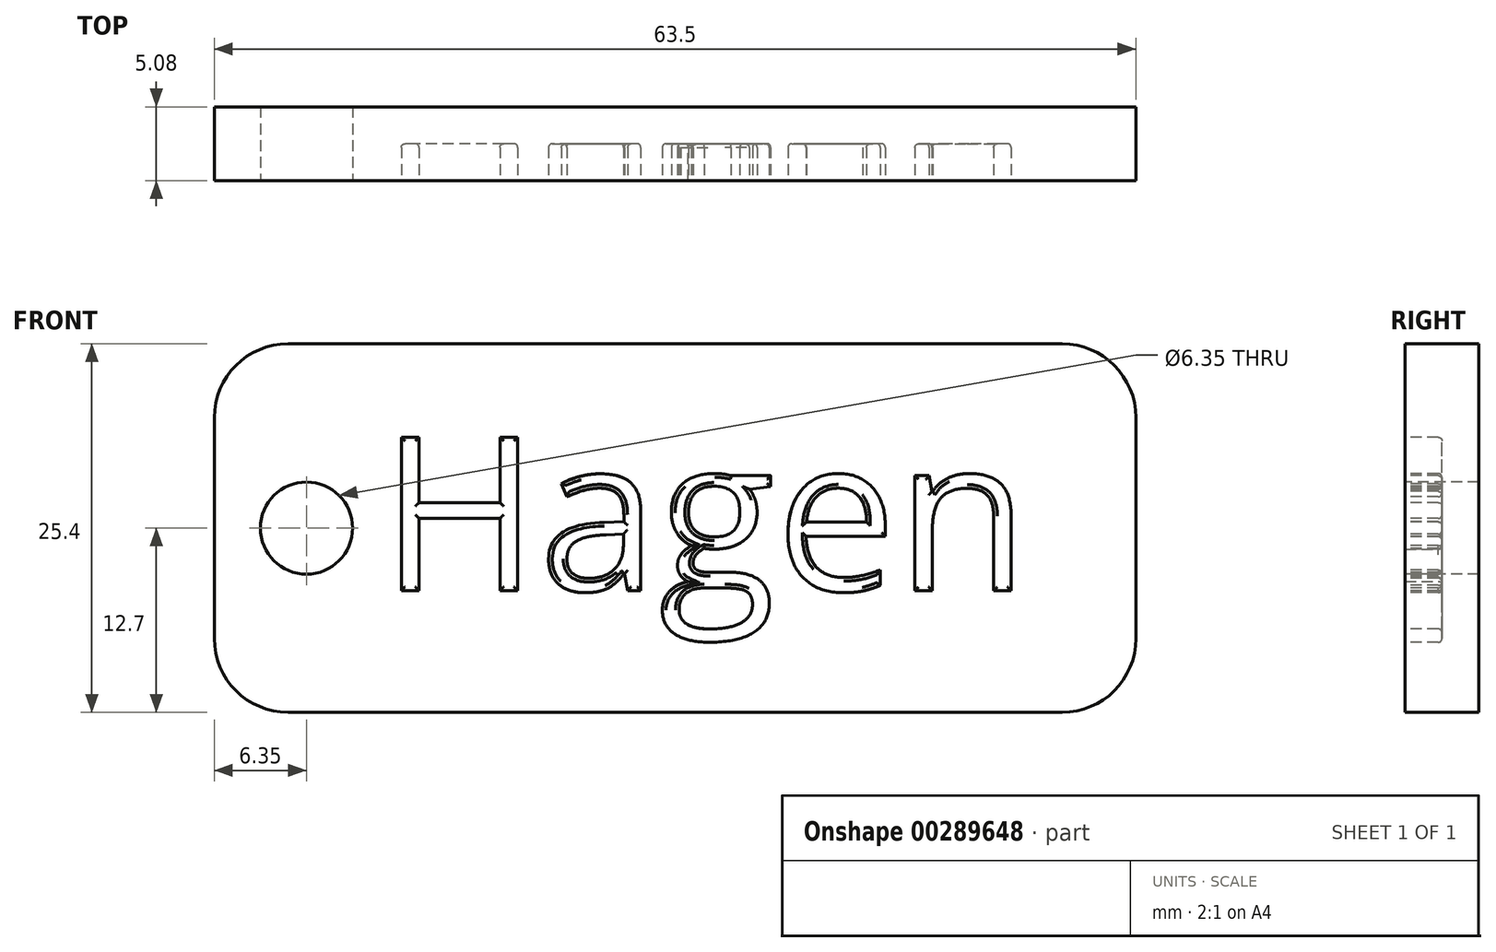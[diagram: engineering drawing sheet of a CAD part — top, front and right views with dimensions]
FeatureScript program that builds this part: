
annotation { "Feature Type Name" : "Feature", "Feature Type Description" : "" }
export const myFeature = defineFeature(function(context is Context, id is Id, definition is map)
    precondition{}
    {
        {
            var Q0;
            Q0=qCreatedBy(makeId("Front.planeOp"),FACE);
            var sketch = newSketch(context, id + "F0", { "sketchPlane" : qUnion([Q0])});
            skLineSegment(sketch, "E0.bottom", {"start": v(-31.75, 12.7) * mm, "end": v(31.75, 12.7) * mm});
            skLineSegment(sketch, "E0.top", {"start": v(-31.75, -12.7) * mm, "end": v(31.75, -12.7) * mm});
            skLineSegment(sketch, "E0.left", {"start": v(-31.75, 12.7) * mm, "end": v(-31.75, -12.7) * mm});
            skLineSegment(sketch, "E0.right", {"start": v(31.75, 12.7) * mm, "end": v(31.75, -12.7) * mm});
            skSolve(sketch);
        }
        {
            var Q0;
            Q0 = qSketchRegion(id + "F0", true);
            extrude(context, id + "F1", {"entities" : qUnion([Q0]), "depth" : 5.08 * mm});
        }
        {
            var Q0;
            Q0=makeQuery(id+"F1.opExtrude","SWEPT_EDGE",EDGE,{"disambiguationData":[OSD([sQuery(id+"F0.wireOp",EDGE,"E0.bottom"),sQuery(id+"F0.wireOp",EDGE,"E0.left")])]});
            var Q1;
            Q1=makeQuery(id+"F1.opExtrude","SWEPT_EDGE",EDGE,{"disambiguationData":[OSD([sQuery(id+"F0.wireOp",EDGE,"E0.bottom"),sQuery(id+"F0.wireOp",EDGE,"E0.right")])]});
            var Q2;
            Q2=makeQuery(id+"F1.opExtrude","SWEPT_EDGE",EDGE,{"disambiguationData":[OSD([sQuery(id+"F0.wireOp",EDGE,"E0.top"),sQuery(id+"F0.wireOp",EDGE,"E0.right")])]});
            var Q3;
            Q3=makeQuery(id+"F1.opExtrude","SWEPT_EDGE",EDGE,{"disambiguationData":[OSD([sQuery(id+"F0.wireOp",EDGE,"E0.top"),sQuery(id+"F0.wireOp",EDGE,"E0.left")])]});
            fillet(context, id + "F2", {"entities" : qUnion([Q0, Q1, Q2, Q3]), "radius" : 5.08 * mm, "tangentPropagation" : true, "allowEdgeOverflow" : false});
        }
        {
            var Q0;
            Q0=makeQuery(id+"F1.opExtrude","CAP_FACE",FACE,{"disambiguationData":[OSD([sQuery(id+"F0.wireOp",EDGE,"E0.bottom"),sQuery(id+"F0.wireOp",EDGE,"E0.top"),sQuery(id+"F0.wireOp",EDGE,"E0.left"),sQuery(id+"F0.wireOp",EDGE,"E0.right")])],"isStart":false});
            var sketch = newSketch(context, id + "F3", { "sketchPlane" : qUnion([Q0])});
            skCircle(sketch, "E1", {"center": v(-25.4, 0) * mm, "radius": 3.17 * mm});
            skSolve(sketch);
        }
        {
            var Q0;
            Q0 = qSketchRegion(id + "F3", true);
            extrude(context, id + "F4", {"entities" : qUnion([Q0]), "operationType" : NewBodyOperationType.REMOVE, "oppositeDirection" : true, "depth" : 5.08 * mm});
        }
        {
            var Q0;
            Q0=makeQuery(id+"F1.opExtrude","CAP_FACE",FACE,{"disambiguationData":[OSD([sQuery(id+"F0.wireOp",EDGE,"E0.bottom"),sQuery(id+"F0.wireOp",EDGE,"E0.top"),sQuery(id+"F0.wireOp",EDGE,"E0.left"),sQuery(id+"F0.wireOp",EDGE,"E0.right")])],"isStart":false});
            var sketch = newSketch(context, id + "F5", { "sketchPlane" : qUnion([Q0])});
            skText(sketch, "E2", { "text": "Hagen", "fontName": "OpenSans-Regular.ttf"});
            const initialGuessF5  = {"E2": [-0.02032, -0.00431, 1, 0, 0.01066]};
            skSetInitialGuess(sketch, initialGuessF5);
            skSolve(sketch);
        }
        {
            var Q0;
            Q0 = qSketchRegion(id + "F5", true);
            extrude(context, id + "F6", {"entities" : qUnion([Q0]), "operationType" : NewBodyOperationType.REMOVE, "oppositeDirection" : true, "depth" : 2.54 * mm});
        }
        {
            var Q0;
            Q0=makeQuery(id+"F6.boolean.opBoolean","COPY",EDGE,{"derivedFrom":makeQuery(id+"F6.opExtrude","CAP_EDGE",EDGE,{"disambiguationData":[OSD([sQuery(id+"F5.wireOp",EDGE,"E2.sketch_text.stroke-34")])],"isStart":false})});
            var Q1;
            Q1=makeQuery(id+"F6.boolean.opBoolean","COPY",EDGE,{"derivedFrom":makeQuery(id+"F6.opExtrude","CAP_EDGE",EDGE,{"disambiguationData":[OSD([sQuery(id+"F5.wireOp",EDGE,"E2.sketch_text.stroke-35")])],"isStart":false})});
            var Q2;
            Q2=makeQuery(id+"F6.boolean.opBoolean","COPY",EDGE,{"derivedFrom":makeQuery(id+"F6.opExtrude","CAP_EDGE",EDGE,{"disambiguationData":[OSD([sQuery(id+"F5.wireOp",EDGE,"E2.sketch_text.stroke-17")])],"isStart":false})});
            var Q3;
            Q3=makeQuery(id+"F6.boolean.opBoolean","COPY",EDGE,{"derivedFrom":makeQuery(id+"F6.opExtrude","CAP_EDGE",EDGE,{"disambiguationData":[OSD([sQuery(id+"F5.wireOp",EDGE,"E2.sketch_text.stroke-12")])],"isStart":false})});
            var Q4;
            Q4=makeQuery(id+"F6.boolean.opBoolean","COPY",EDGE,{"derivedFrom":makeQuery(id+"F6.opExtrude","CAP_EDGE",EDGE,{"disambiguationData":[OSD([sQuery(id+"F5.wireOp",EDGE,"E2.sketch_text.stroke-23")])],"isStart":false})});
            var Q5;
            Q5=makeQuery(id+"F6.boolean.opBoolean","COPY",EDGE,{"derivedFrom":makeQuery(id+"F6.opExtrude","CAP_EDGE",EDGE,{"disambiguationData":[OSD([sQuery(id+"F5.wireOp",EDGE,"E2.sketch_text.stroke-22")])],"isStart":false})});
            var Q6;
            Q6=makeQuery(id+"F6.boolean.opBoolean","COPY",EDGE,{"derivedFrom":makeQuery(id+"F6.opExtrude","CAP_EDGE",EDGE,{"disambiguationData":[OSD([sQuery(id+"F5.wireOp",EDGE,"E2.sketch_text.stroke-24")])],"isStart":false})});
            var Q7;
            Q7=makeQuery(id+"F6.boolean.opBoolean","COPY",EDGE,{"derivedFrom":makeQuery(id+"F6.opExtrude","CAP_EDGE",EDGE,{"disambiguationData":[OSD([sQuery(id+"F5.wireOp",EDGE,"E2.sketch_text.stroke-9")])],"isStart":false})});
            var Q8;
            Q8=makeQuery(id+"F6.boolean.opBoolean","COPY",EDGE,{"derivedFrom":makeQuery(id+"F6.opExtrude","CAP_EDGE",EDGE,{"disambiguationData":[OSD([sQuery(id+"F5.wireOp",EDGE,"E2.sketch_text.stroke-2")])],"isStart":false})});
            var Q9;
            Q9=makeQuery(id+"F6.boolean.opBoolean","COPY",EDGE,{"derivedFrom":makeQuery(id+"F6.opExtrude","CAP_EDGE",EDGE,{"disambiguationData":[OSD([sQuery(id+"F5.wireOp",EDGE,"E2.sketch_text.stroke-5")])],"isStart":false})});
            var Q10;
            Q10=makeQuery(id+"F6.boolean.opBoolean","COPY",EDGE,{"derivedFrom":makeQuery(id+"F6.opExtrude","CAP_EDGE",EDGE,{"disambiguationData":[OSD([sQuery(id+"F5.wireOp",EDGE,"E2.sketch_text.stroke-25")])],"isStart":false})});
            var Q11;
            Q11=makeQuery(id+"F6.boolean.opBoolean","COPY",EDGE,{"derivedFrom":makeQuery(id+"F6.opExtrude","CAP_EDGE",EDGE,{"disambiguationData":[OSD([sQuery(id+"F5.wireOp",EDGE,"E2.sketch_text.stroke-26")])],"isStart":false})});
            var Q12;
            Q12=makeQuery(id+"F6.boolean.opBoolean","COPY",EDGE,{"derivedFrom":makeQuery(id+"F6.opExtrude","CAP_EDGE",EDGE,{"disambiguationData":[OSD([sQuery(id+"F5.wireOp",EDGE,"E2.sketch_text.stroke-30")])],"isStart":false})});
            var Q13;
            Q13=makeQuery(id+"F6.boolean.opBoolean","COPY",EDGE,{"derivedFrom":makeQuery(id+"F6.opExtrude","CAP_EDGE",EDGE,{"disambiguationData":[OSD([sQuery(id+"F5.wireOp",EDGE,"E2.sketch_text.stroke-6")])],"isStart":false})});
            var Q14;
            Q14=makeQuery(id+"F6.boolean.opBoolean","COPY",EDGE,{"derivedFrom":makeQuery(id+"F6.opExtrude","CAP_EDGE",EDGE,{"disambiguationData":[OSD([sQuery(id+"F5.wireOp",EDGE,"E2.sketch_text.stroke-7")])],"isStart":false})});
            var Q15;
            Q15=makeQuery(id+"F6.boolean.opBoolean","COPY",EDGE,{"derivedFrom":makeQuery(id+"F6.opExtrude","CAP_EDGE",EDGE,{"disambiguationData":[OSD([sQuery(id+"F5.wireOp",EDGE,"E2.sketch_text.stroke-3")])],"isStart":false})});
            var Q16;
            Q16=makeQuery(id+"F6.boolean.opBoolean","COPY",EDGE,{"derivedFrom":makeQuery(id+"F6.opExtrude","CAP_EDGE",EDGE,{"disambiguationData":[OSD([sQuery(id+"F5.wireOp",EDGE,"E2.sketch_text.stroke-4")])],"isStart":false})});
            var Q17;
            Q17=makeQuery(id+"F6.boolean.opBoolean","COPY",EDGE,{"derivedFrom":makeQuery(id+"F6.opExtrude","CAP_EDGE",EDGE,{"disambiguationData":[OSD([sQuery(id+"F5.wireOp",EDGE,"E2.sketch_text.stroke-0")])],"isStart":false})});
            var Q18;
            Q18=makeQuery(id+"F6.boolean.opBoolean","COPY",EDGE,{"derivedFrom":makeQuery(id+"F6.opExtrude","CAP_EDGE",EDGE,{"disambiguationData":[OSD([sQuery(id+"F5.wireOp",EDGE,"E2.sketch_text.stroke-11")])],"isStart":false})});
            var Q19;
            Q19=makeQuery(id+"F6.boolean.opBoolean","COPY",EDGE,{"derivedFrom":makeQuery(id+"F6.opExtrude","CAP_EDGE",EDGE,{"disambiguationData":[OSD([sQuery(id+"F5.wireOp",EDGE,"E2.sketch_text.stroke-10")])],"isStart":false})});
            var Q20;
            Q20=makeQuery(id+"F6.boolean.opBoolean","COPY",EDGE,{"derivedFrom":makeQuery(id+"F6.opExtrude","CAP_EDGE",EDGE,{"disambiguationData":[OSD([sQuery(id+"F5.wireOp",EDGE,"E2.sketch_text.stroke-8")])],"isStart":false})});
            var Q21;
            Q21=makeQuery(id+"F6.boolean.opBoolean","COPY",EDGE,{"derivedFrom":makeQuery(id+"F6.opExtrude","CAP_EDGE",EDGE,{"disambiguationData":[OSD([sQuery(id+"F5.wireOp",EDGE,"E2.sketch_text.stroke-1")])],"isStart":false})});
            var Q22;
            Q22=makeQuery(id+"F6.boolean.opBoolean","COPY",EDGE,{"derivedFrom":makeQuery(id+"F6.opExtrude","CAP_EDGE",EDGE,{"disambiguationData":[OSD([sQuery(id+"F5.wireOp",EDGE,"E2.sketch_text.stroke-89")])],"isStart":false})});
            var Q23;
            Q23=makeQuery(id+"F6.boolean.opBoolean","COPY",EDGE,{"derivedFrom":makeQuery(id+"F6.opExtrude","CAP_EDGE",EDGE,{"disambiguationData":[OSD([sQuery(id+"F5.wireOp",EDGE,"E2.sketch_text.stroke-91")])],"isStart":false})});
            var Q24;
            Q24=makeQuery(id+"F6.boolean.opBoolean","COPY",EDGE,{"derivedFrom":makeQuery(id+"F6.opExtrude","CAP_EDGE",EDGE,{"disambiguationData":[OSD([sQuery(id+"F5.wireOp",EDGE,"E2.sketch_text.stroke-94")])],"isStart":false})});
            var Q25;
            Q25=makeQuery(id+"F6.boolean.opBoolean","COPY",EDGE,{"derivedFrom":makeQuery(id+"F6.opExtrude","CAP_EDGE",EDGE,{"disambiguationData":[OSD([sQuery(id+"F5.wireOp",EDGE,"E2.sketch_text.stroke-98")])],"isStart":false})});
            var Q26;
            Q26=makeQuery(id+"F6.boolean.opBoolean","COPY",EDGE,{"derivedFrom":makeQuery(id+"F6.opExtrude","CAP_EDGE",EDGE,{"disambiguationData":[OSD([sQuery(id+"F5.wireOp",EDGE,"E2.sketch_text.stroke-99")])],"isStart":false})});
            var Q27;
            Q27=makeQuery(id+"F6.boolean.opBoolean","COPY",EDGE,{"derivedFrom":makeQuery(id+"F6.opExtrude","CAP_EDGE",EDGE,{"disambiguationData":[OSD([sQuery(id+"F5.wireOp",EDGE,"E2.sketch_text.stroke-90")])],"isStart":false})});
            var Q28;
            Q28=makeQuery(id+"F6.boolean.opBoolean","COPY",EDGE,{"derivedFrom":makeQuery(id+"F6.opExtrude","CAP_EDGE",EDGE,{"disambiguationData":[OSD([sQuery(id+"F5.wireOp",EDGE,"E2.sketch_text.stroke-65")])],"isStart":false})});
            var Q29;
            Q29=makeQuery(id+"F6.boolean.opBoolean","COPY",EDGE,{"derivedFrom":makeQuery(id+"F6.opExtrude","CAP_EDGE",EDGE,{"disambiguationData":[OSD([sQuery(id+"F5.wireOp",EDGE,"E2.sketch_text.stroke-66")])],"isStart":false})});
            var Q30;
            Q30=makeQuery(id+"F6.boolean.opBoolean","COPY",EDGE,{"derivedFrom":makeQuery(id+"F6.opExtrude","CAP_EDGE",EDGE,{"disambiguationData":[OSD([sQuery(id+"F5.wireOp",EDGE,"E2.sketch_text.stroke-67")])],"isStart":false})});
            var Q31;
            Q31=makeQuery(id+"F6.boolean.opBoolean","COPY",FACE,{"derivedFrom":makeQuery(id+"F6.opExtrude","CAP_FACE",FACE,{"disambiguationData":[OSD([sQuery(id+"F5.wireOp",EDGE,"E2.sketch_text.stroke-39"),sQuery(id+"F5.wireOp",EDGE,"E2.sketch_text.stroke-40"),sQuery(id+"F5.wireOp",EDGE,"E2.sketch_text.stroke-41"),sQuery(id+"F5.wireOp",EDGE,"E2.sketch_text.stroke-42"),sQuery(id+"F5.wireOp",EDGE,"E2.sketch_text.stroke-43"),sQuery(id+"F5.wireOp",EDGE,"E2.sketch_text.stroke-44"),sQuery(id+"F5.wireOp",EDGE,"E2.sketch_text.stroke-45"),sQuery(id+"F5.wireOp",EDGE,"E2.sketch_text.stroke-46"),sQuery(id+"F5.wireOp",EDGE,"E2.sketch_text.stroke-47"),sQuery(id+"F5.wireOp",EDGE,"E2.sketch_text.stroke-48"),sQuery(id+"F5.wireOp",EDGE,"E2.sketch_text.stroke-49"),sQuery(id+"F5.wireOp",EDGE,"E2.sketch_text.stroke-50"),sQuery(id+"F5.wireOp",EDGE,"E2.sketch_text.stroke-51"),sQuery(id+"F5.wireOp",EDGE,"E2.sketch_text.stroke-52"),sQuery(id+"F5.wireOp",EDGE,"E2.sketch_text.stroke-53"),sQuery(id+"F5.wireOp",EDGE,"E2.sketch_text.stroke-54"),sQuery(id+"F5.wireOp",EDGE,"E2.sketch_text.stroke-55"),sQuery(id+"F5.wireOp",EDGE,"E2.sketch_text.stroke-56"),sQuery(id+"F5.wireOp",EDGE,"E2.sketch_text.stroke-57"),sQuery(id+"F5.wireOp",EDGE,"E2.sketch_text.stroke-58"),sQuery(id+"F5.wireOp",EDGE,"E2.sketch_text.stroke-59"),sQuery(id+"F5.wireOp",EDGE,"E2.sketch_text.stroke-60"),sQuery(id+"F5.wireOp",EDGE,"E2.sketch_text.stroke-61"),sQuery(id+"F5.wireOp",EDGE,"E2.sketch_text.stroke-62"),sQuery(id+"F5.wireOp",EDGE,"E2.sketch_text.stroke-63"),sQuery(id+"F5.wireOp",EDGE,"E2.sketch_text.stroke-64"),sQuery(id+"F5.wireOp",EDGE,"E2.sketch_text.stroke-65"),sQuery(id+"F5.wireOp",EDGE,"E2.sketch_text.stroke-66"),sQuery(id+"F5.wireOp",EDGE,"E2.sketch_text.stroke-67"),sQuery(id+"F5.wireOp",EDGE,"E2.sketch_text.stroke-68"),sQuery(id+"F5.wireOp",EDGE,"E2.sketch_text.stroke-69"),sQuery(id+"F5.wireOp",EDGE,"E2.sketch_text.stroke-70"),sQuery(id+"F5.wireOp",EDGE,"E2.sketch_text.stroke-71"),sQuery(id+"F5.wireOp",EDGE,"E2.sketch_text.stroke-72"),sQuery(id+"F5.wireOp",EDGE,"E2.sketch_text.stroke-73"),sQuery(id+"F5.wireOp",EDGE,"E2.sketch_text.stroke-74"),sQuery(id+"F5.wireOp",EDGE,"E2.sketch_text.stroke-75"),sQuery(id+"F5.wireOp",EDGE,"E2.sketch_text.stroke-76"),sQuery(id+"F5.wireOp",EDGE,"E2.sketch_text.stroke-77"),sQuery(id+"F5.wireOp",EDGE,"E2.sketch_text.stroke-78"),sQuery(id+"F5.wireOp",EDGE,"E2.sketch_text.stroke-79"),sQuery(id+"F5.wireOp",EDGE,"E2.sketch_text.stroke-80"),sQuery(id+"F5.wireOp",EDGE,"E2.sketch_text.stroke-81"),sQuery(id+"F5.wireOp",EDGE,"E2.sketch_text.stroke-82")])],"isStart":false})});
            var Q32;
            Q32=makeQuery(id+"F6.boolean.opBoolean","COPY",FACE,{"derivedFrom":makeQuery(id+"F6.opExtrude","CAP_FACE",FACE,{"disambiguationData":[OSD([sQuery(id+"F5.wireOp",EDGE,"E2.sketch_text.stroke-83"),sQuery(id+"F5.wireOp",EDGE,"E2.sketch_text.stroke-84"),sQuery(id+"F5.wireOp",EDGE,"E2.sketch_text.stroke-85"),sQuery(id+"F5.wireOp",EDGE,"E2.sketch_text.stroke-86"),sQuery(id+"F5.wireOp",EDGE,"E2.sketch_text.stroke-87"),sQuery(id+"F5.wireOp",EDGE,"E2.sketch_text.stroke-88"),sQuery(id+"F5.wireOp",EDGE,"E2.sketch_text.stroke-89"),sQuery(id+"F5.wireOp",EDGE,"E2.sketch_text.stroke-90"),sQuery(id+"F5.wireOp",EDGE,"E2.sketch_text.stroke-91"),sQuery(id+"F5.wireOp",EDGE,"E2.sketch_text.stroke-92"),sQuery(id+"F5.wireOp",EDGE,"E2.sketch_text.stroke-93"),sQuery(id+"F5.wireOp",EDGE,"E2.sketch_text.stroke-94"),sQuery(id+"F5.wireOp",EDGE,"E2.sketch_text.stroke-95"),sQuery(id+"F5.wireOp",EDGE,"E2.sketch_text.stroke-96"),sQuery(id+"F5.wireOp",EDGE,"E2.sketch_text.stroke-97"),sQuery(id+"F5.wireOp",EDGE,"E2.sketch_text.stroke-98"),sQuery(id+"F5.wireOp",EDGE,"E2.sketch_text.stroke-99"),sQuery(id+"F5.wireOp",EDGE,"E2.sketch_text.stroke-100"),sQuery(id+"F5.wireOp",EDGE,"E2.sketch_text.stroke-101")])],"isStart":false})});
            var Q33;
            Q33=makeQuery(id+"F6.boolean.opBoolean","COPY",FACE,{"derivedFrom":makeQuery(id+"F6.opExtrude","CAP_FACE",FACE,{"disambiguationData":[OSD([sQuery(id+"F5.wireOp",EDGE,"E2.sketch_text.stroke-102"),sQuery(id+"F5.wireOp",EDGE,"E2.sketch_text.stroke-103"),sQuery(id+"F5.wireOp",EDGE,"E2.sketch_text.stroke-104"),sQuery(id+"F5.wireOp",EDGE,"E2.sketch_text.stroke-105"),sQuery(id+"F5.wireOp",EDGE,"E2.sketch_text.stroke-106"),sQuery(id+"F5.wireOp",EDGE,"E2.sketch_text.stroke-107"),sQuery(id+"F5.wireOp",EDGE,"E2.sketch_text.stroke-108"),sQuery(id+"F5.wireOp",EDGE,"E2.sketch_text.stroke-109"),sQuery(id+"F5.wireOp",EDGE,"E2.sketch_text.stroke-110"),sQuery(id+"F5.wireOp",EDGE,"E2.sketch_text.stroke-111"),sQuery(id+"F5.wireOp",EDGE,"E2.sketch_text.stroke-112"),sQuery(id+"F5.wireOp",EDGE,"E2.sketch_text.stroke-113"),sQuery(id+"F5.wireOp",EDGE,"E2.sketch_text.stroke-114"),sQuery(id+"F5.wireOp",EDGE,"E2.sketch_text.stroke-115"),sQuery(id+"F5.wireOp",EDGE,"E2.sketch_text.stroke-116"),sQuery(id+"F5.wireOp",EDGE,"E2.sketch_text.stroke-117"),sQuery(id+"F5.wireOp",EDGE,"E2.sketch_text.stroke-118")])],"isStart":false})});
            var Q34;
            Q34=makeQuery(id+"F6.boolean.opBoolean","COPY",EDGE,{"derivedFrom":makeQuery(id+"F6.opExtrude","CAP_EDGE",EDGE,{"disambiguationData":[OSD([sQuery(id+"F5.wireOp",EDGE,"E2.sketch_text.stroke-29")])],"isStart":false})});
            var Q35;
            Q35=makeQuery(id+"F6.boolean.opBoolean","COPY",FACE,{"derivedFrom":makeQuery(id+"F6.opExtrude","CAP_FACE",FACE,{"disambiguationData":[OSD([sQuery(id+"F5.wireOp",EDGE,"E2.sketch_text.stroke-12"),sQuery(id+"F5.wireOp",EDGE,"E2.sketch_text.stroke-13"),sQuery(id+"F5.wireOp",EDGE,"E2.sketch_text.stroke-14"),sQuery(id+"F5.wireOp",EDGE,"E2.sketch_text.stroke-15"),sQuery(id+"F5.wireOp",EDGE,"E2.sketch_text.stroke-16"),sQuery(id+"F5.wireOp",EDGE,"E2.sketch_text.stroke-17"),sQuery(id+"F5.wireOp",EDGE,"E2.sketch_text.stroke-18"),sQuery(id+"F5.wireOp",EDGE,"E2.sketch_text.stroke-19"),sQuery(id+"F5.wireOp",EDGE,"E2.sketch_text.stroke-20"),sQuery(id+"F5.wireOp",EDGE,"E2.sketch_text.stroke-21"),sQuery(id+"F5.wireOp",EDGE,"E2.sketch_text.stroke-22"),sQuery(id+"F5.wireOp",EDGE,"E2.sketch_text.stroke-23"),sQuery(id+"F5.wireOp",EDGE,"E2.sketch_text.stroke-24"),sQuery(id+"F5.wireOp",EDGE,"E2.sketch_text.stroke-25"),sQuery(id+"F5.wireOp",EDGE,"E2.sketch_text.stroke-26"),sQuery(id+"F5.wireOp",EDGE,"E2.sketch_text.stroke-27"),sQuery(id+"F5.wireOp",EDGE,"E2.sketch_text.stroke-28"),sQuery(id+"F5.wireOp",EDGE,"E2.sketch_text.stroke-29"),sQuery(id+"F5.wireOp",EDGE,"E2.sketch_text.stroke-30"),sQuery(id+"F5.wireOp",EDGE,"E2.sketch_text.stroke-31"),sQuery(id+"F5.wireOp",EDGE,"E2.sketch_text.stroke-32"),sQuery(id+"F5.wireOp",EDGE,"E2.sketch_text.stroke-33"),sQuery(id+"F5.wireOp",EDGE,"E2.sketch_text.stroke-34"),sQuery(id+"F5.wireOp",EDGE,"E2.sketch_text.stroke-35"),sQuery(id+"F5.wireOp",EDGE,"E2.sketch_text.stroke-36"),sQuery(id+"F5.wireOp",EDGE,"E2.sketch_text.stroke-37"),sQuery(id+"F5.wireOp",EDGE,"E2.sketch_text.stroke-38")])],"isStart":false})});
            fillet(context, id + "F7", {"entities" : qUnion([Q0, Q1, Q2, Q3, Q4, Q5, Q6, Q7, Q8, Q9, Q10, Q11, Q12, Q13, Q14, Q15, Q16, Q17, Q18, Q19, Q20, Q21, Q22, Q23, Q24, Q25, Q26, Q27, Q28, Q29, Q30, Q31, Q32, Q33, Q34, Q35]), "radius" : 0.25 * mm, "tangentPropagation" : true, "allowEdgeOverflow" : false});
        }
    });
